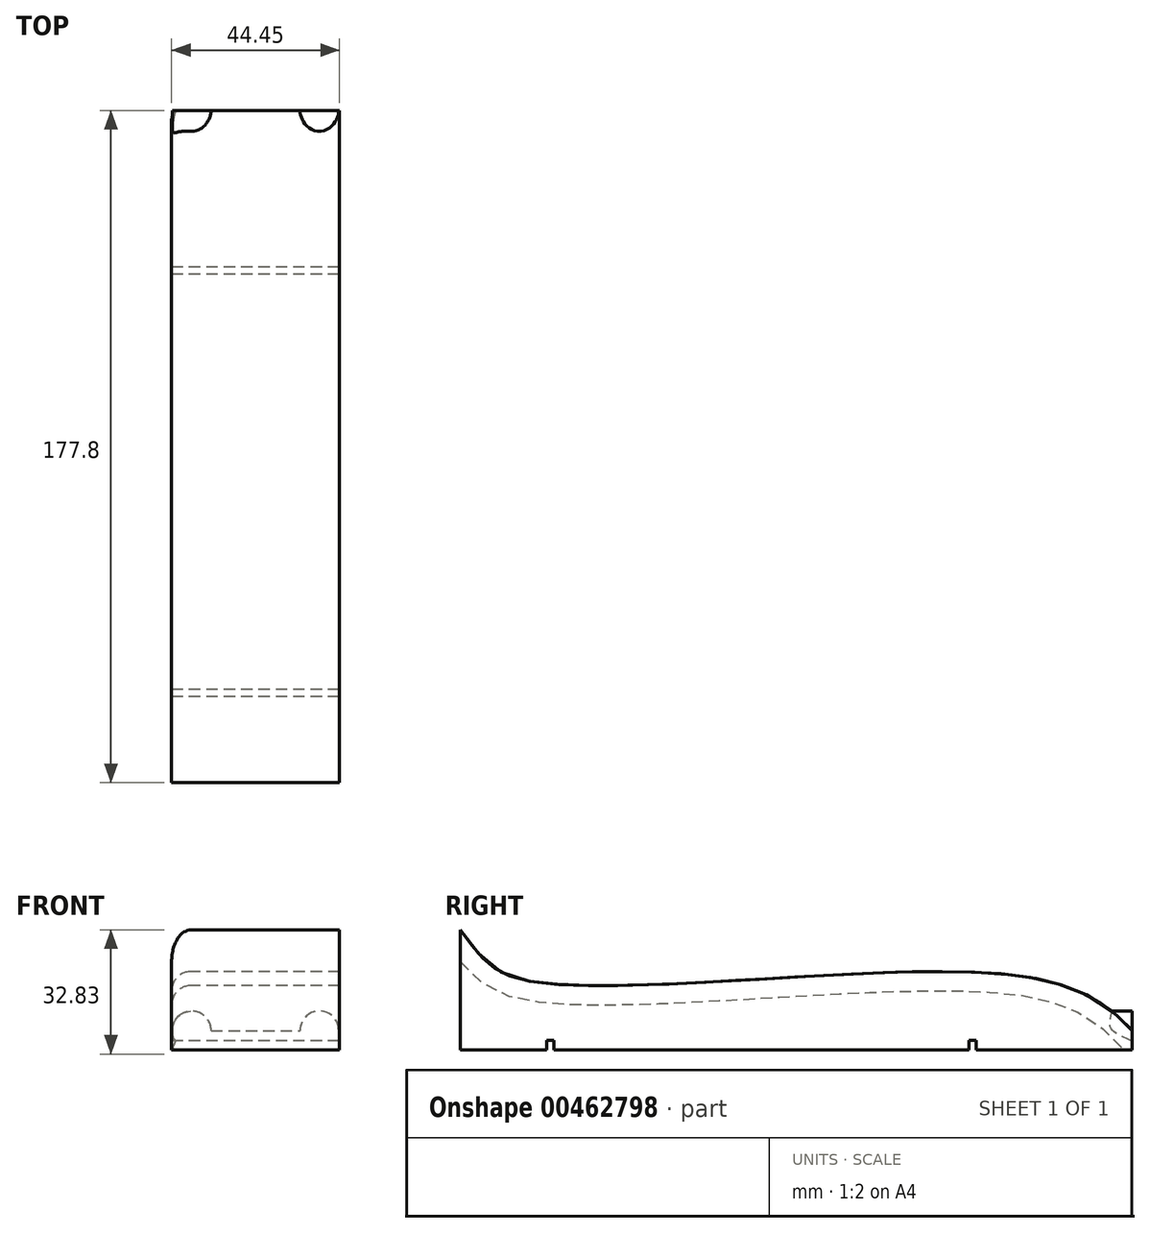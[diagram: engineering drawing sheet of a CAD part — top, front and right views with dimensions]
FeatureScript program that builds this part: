
annotation { "Feature Type Name" : "Feature", "Feature Type Description" : "" }
export const myFeature = defineFeature(function(context is Context, id is Id, definition is map)
    precondition{}
    {
        {
            var Q0;
            Q0=qCreatedBy(makeId("Top.planeOp"),FACE);
            var sketch = newSketch(context, id + "F0", { "sketchPlane" : qUnion([Q0])});
            skLineSegment(sketch, "E0.bottom", {"start": v(0, 0) * mm, "end": v(44.45, 0) * mm});
            skLineSegment(sketch, "E0.top", {"start": v(0, 177.8) * mm, "end": v(44.45, 177.8) * mm});
            skLineSegment(sketch, "E0.left", {"start": v(0, 0) * mm, "end": v(0, 177.8) * mm});
            skLineSegment(sketch, "E0.right", {"start": v(44.45, 0) * mm, "end": v(44.45, 177.8) * mm});
            skSolve(sketch);
        }
        {
            var Q0;
            Q0 = qSketchRegion(id + "F0", true);
            extrude(context, id + "F1", {"entities" : qUnion([Q0]), "depth" : 31.75 * mm});
        }
        {
            var Q0;
            Q0=makeQuery(id+"F1.opExtrude","CAP_FACE",FACE,{"disambiguationData":[OSD([sQuery(id+"F0.wireOp",EDGE,"E0.bottom"),sQuery(id+"F0.wireOp",EDGE,"E0.top"),sQuery(id+"F0.wireOp",EDGE,"E0.left"),sQuery(id+"F0.wireOp",EDGE,"E0.right")])],"isStart":true});
            var sketch = newSketch(context, id + "F2", { "sketchPlane" : qUnion([Q0])});
            skLineSegment(sketch, "E1.bottom", {"start": v(0, -22.86) * mm, "end": v(44.45, -22.86) * mm});
            skLineSegment(sketch, "E1.top", {"start": v(0, -24.76) * mm, "end": v(44.45, -24.76) * mm});
            skLineSegment(sketch, "E1.left", {"start": v(0, -22.86) * mm, "end": v(0, -24.76) * mm});
            skLineSegment(sketch, "E1.right", {"start": v(44.45, -22.86) * mm, "end": v(44.45, -24.76) * mm});
            skLineSegment(sketch, "E2.bottom", {"start": v(0, -134.62) * mm, "end": v(44.45, -134.62) * mm});
            skLineSegment(sketch, "E2.top", {"start": v(0, -136.53) * mm, "end": v(44.45, -136.53) * mm});
            skLineSegment(sketch, "E2.left", {"start": v(0, -134.62) * mm, "end": v(0, -136.53) * mm});
            skLineSegment(sketch, "E2.right", {"start": v(44.45, -134.62) * mm, "end": v(44.45, -136.53) * mm});
            skSolve(sketch);
        }
        {
            var Q0;
            Q0 = qSketchRegion(id + "F2", true);
            extrude(context, id + "F3", {"entities" : qUnion([Q0]), "operationType" : NewBodyOperationType.REMOVE, "depth" : -2.54 * mm});
        }
        {
            var Q0;
            Q0=makeQuery(id+"F1.opExtrude","SWEPT_FACE",FACE,{"disambiguationData":[OSD([sQuery(id+"F0.wireOp",EDGE,"E0.right")])]});
            var sketch = newSketch(context, id + "F4", { "sketchPlane" : qUnion([Q0])});
            skLineSegment(sketch, "E3", {"start": v(0, 31.75) * mm, "end": v(177.8, 31.75) * mm});
            skLineSegment(sketch, "E4", {"start": v(177.8, 31.75) * mm, "end": v(177.8, 5.14) * mm});
            skFitSpline(sketch, "E5", {"points": [v(0, 31.75) * mm, v(17.79, 18.31) * mm, v(138.84, 20.48) * mm, v(177.8, 5.14) * mm], "startDerivative": vector(77.82, -103.02) * mm, "endDerivative": vector(90.9, -98.4) * mm});
            skSolve(sketch);
        }
        {
            var Q0;
            Q0 = qSketchRegion(id + "F4", true);
            extrude(context, id + "F5", {"entities" : qUnion([Q0]), "operationType" : NewBodyOperationType.REMOVE, "oppositeDirection" : true, "depth" : 50.8 * mm});
        }
        {
            var Q0;
            Q0=makeQuery(id+"F1.opExtrude","SWEPT_FACE",FACE,{"disambiguationData":[OSD([sQuery(id+"F0.wireOp",EDGE,"E0.top")])]});
            var sketch = newSketch(context, id + "F6", { "sketchPlane" : qUnion([Q0])});
            skCircle(sketch, "E6", {"center": v(-39.12, 5.14) * mm, "radius": 5.14 * mm});
            skCircle(sketch, "E7", {"center": v(-5.33, 5.14) * mm, "radius": 5.14 * mm});
            skSolve(sketch);
        }
        {
            var Q0;
            Q0 = qSketchRegion(id + "F6", true);
            extrude(context, id + "F7", {"entities" : qUnion([Q0]), "operationType" : NewBodyOperationType.ADD, "oppositeDirection" : true, "depth" : 25.4 * mm});
        }
        {
            var Q0;
            Q0=makeQuery(id+"F5.boolean.opBoolean","INTERSECT",EDGE,{"derivedFrom":[makeQuery(id+"F1.opExtrude","SWEPT_FACE",FACE,{"disambiguationData":[OSD([sQuery(id+"F0.wireOp",EDGE,"E0.left")])]}),makeQuery(id+"F5.opExtrude","SWEPT_FACE",FACE,{"disambiguationData":[OSD([sQuery(id+"F4.wireOp",EDGE,"E5")])]})]});
            var Q1;
            Q1=makeQuery(id+"F5.boolean.opBoolean","COPY",EDGE,{"derivedFrom":makeQuery(id+"F5.opExtrude","CAP_EDGE",EDGE,{"disambiguationData":[OSD([sQuery(id+"F4.wireOp",EDGE,"E5")])],"isStart":true})});
            var Q2;
            {var subQ0=sQuery(id+"F6.wireOp",EDGE,"E6");var subQ1=sQuery(id+"F4.wireOp",EDGE,"E5");var subQ2=sQuery(id+"F0.wireOp",EDGE,"E0.top");var subQ3=sQuery(id+"F6.wireOp",EDGE,"E7");Q2=makeQuery(id+"F7.boolean.opBoolean","SPLIT",EDGE,{"disambiguationData":[TD([makeQuery(id+"F1.opExtrude","SWEPT_FACE",FACE,{"disambiguationData":[OSD([subQ2])]}),makeQuery(id+"F5.boolean.opBoolean","COPY",FACE,{"derivedFrom":makeQuery(id+"F5.opExtrude","SWEPT_FACE",FACE,{"disambiguationData":[OSD([subQ1])]})}),makeQuery(id+"F7.opExtrude","SWEPT_FACE",FACE,{"disambiguationData":[OSD([subQ0])]}),makeQuery(id+"F7.opExtrude","CAP_FACE",FACE,{"disambiguationData":[OSD([subQ0])],"isStart":true}),makeQuery(id+"F7.opExtrude","SWEPT_FACE",FACE,{"disambiguationData":[OSD([subQ3])]}),makeQuery(id+"F7.opExtrude","CAP_FACE",FACE,{"disambiguationData":[OSD([subQ3])],"isStart":true})])],"derivedFrom":makeQuery(id+"F5.boolean.opBoolean","COPY",EDGE,{"derivedFrom":makeQuery(id+"F5.opExtrude","SWEPT_EDGE",EDGE,{"disambiguationData":[OSD([subQ2,sQuery(id+"F0.wireOp",EDGE,"E0.right"),sQuery(id+"F4.wireOp",EDGE,"E4"),subQ1])]})})});}
            fillet(context, id + "F8", {"entities" : qUnion([Q0, Q1, Q2]), "radius" : 5.08 * mm, "tangentPropagation" : true, "allowEdgeOverflow" : false});
        }
    });
